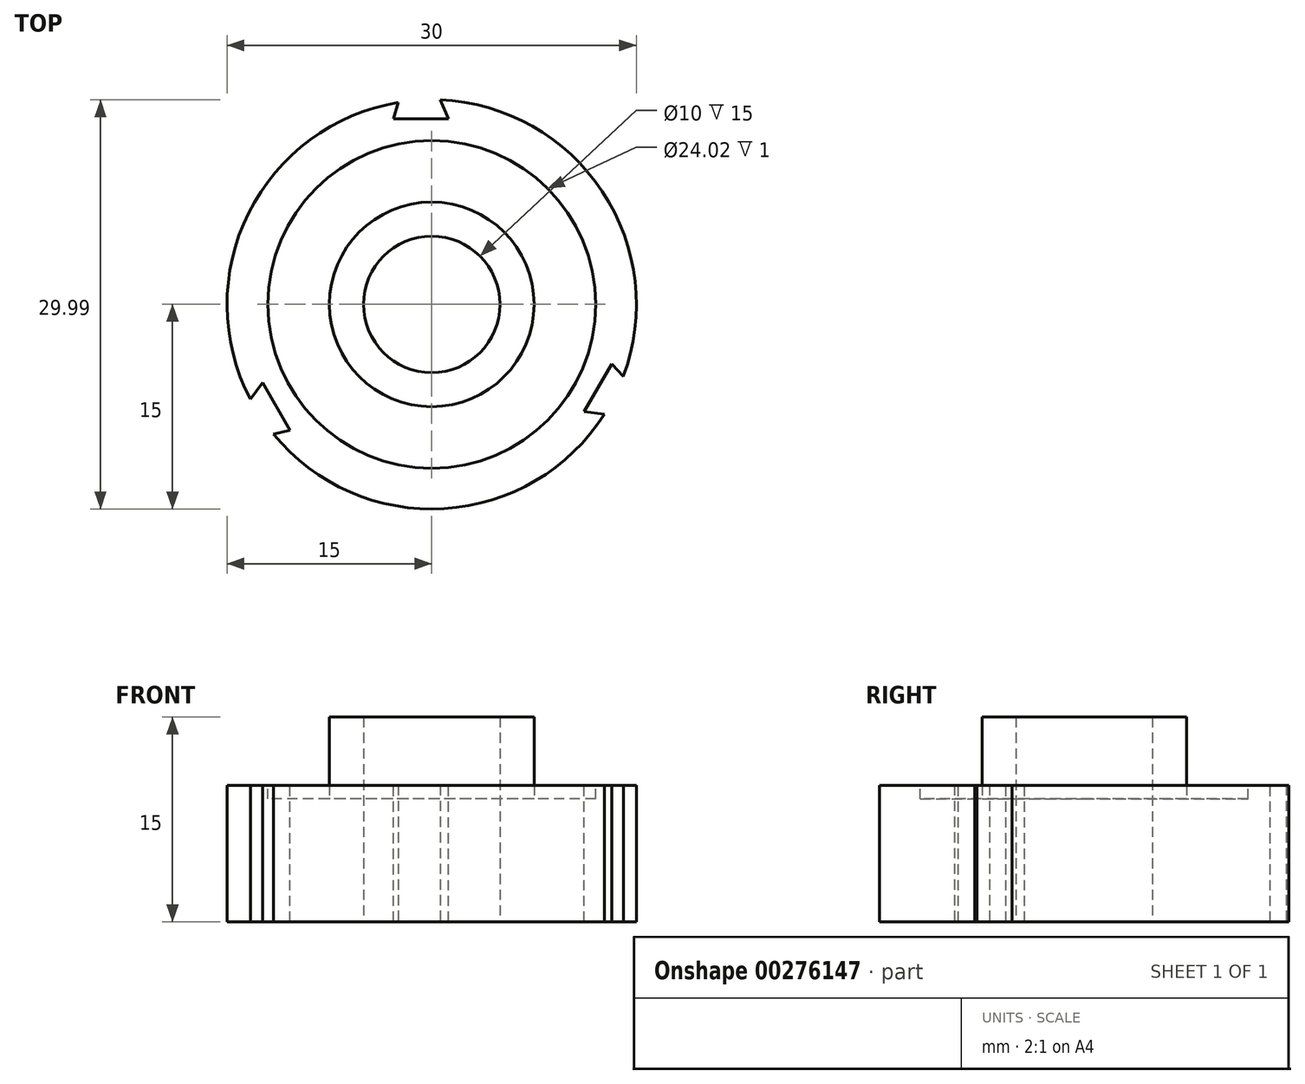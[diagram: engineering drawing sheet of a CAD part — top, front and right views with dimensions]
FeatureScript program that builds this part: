
annotation { "Feature Type Name" : "Feature", "Feature Type Description" : "" }
export const myFeature = defineFeature(function(context is Context, id is Id, definition is map)
    precondition{}
    {
        {
            var Q0;
            Q0=qCreatedBy(makeId("Top.planeOp"),FACE);
            var sketch = newSketch(context, id + "F0", { "sketchPlane" : qUnion([Q0])});
            skCircle(sketch, "E0", {"center": v(0, 0) * mm, "radius": 15 * mm});
            skCircle(sketch, "E1", {"center": v(0, 0) * mm, "radius": 5 * mm});
            skSolve(sketch);
        }
        {
            var Q0;
            Q0 = qSketchRegion(id + "F0", true);
            extrude(context, id + "F1", {"entities" : qUnion([Q0]), "depth" : 10 * mm});
        }
        {
            var Q0;
            Q0=makeQuery(id+"F1.opExtrude","CAP_FACE",FACE,{"disambiguationData":[OSD([sQuery(id+"F0.wireOp",EDGE,"E0"),sQuery(id+"F0.wireOp",EDGE,"E1")])],"isStart":false});
            var sketch = newSketch(context, id + "F2", { "sketchPlane" : qUnion([Q0])});
            skCircle(sketch, "E2", {"center": v(0, 0) * mm, "radius": 7.5 * mm});
            skCircle(sketch, "E3", {"center": v(0, 0) * mm, "radius": 5 * mm});
            skSolve(sketch);
        }
        {
            var Q0;
            Q0=makeQuery(id+"F2.imprint","IMPRINT",FACE,{"disambiguationData":[TD([[makeQuery(id+"F2.imprint","IMPRINT",EDGE,{"derivedFrom":sQuery(id+"F2.wireOp",EDGE,"E2")}),1.0]])]});
            extrude(context, id + "F3", {"entities" : qUnion([Q0]), "operationType" : NewBodyOperationType.ADD, "depth" : 5 * mm});
        }
        {
            var Q0;
            Q0=makeQuery(id+"F1.opExtrude","CAP_FACE",FACE,{"disambiguationData":[OSD([sQuery(id+"F0.wireOp",EDGE,"E0"),sQuery(id+"F0.wireOp",EDGE,"E1")])],"isStart":false});
            var sketch = newSketch(context, id + "F4", { "sketchPlane" : qUnion([Q0])});
            skCircle(sketch, "E4", {"center": v(0, 0) * mm, "radius": 12.01 * mm});
            skCircle(sketch, "E5", {"center": v(0, 0) * mm, "radius": 11.23 * mm});
            skSolve(sketch);
        }
        {
            var Q0;
            Q0=makeQuery(id+"F4.imprint","IMPRINT",FACE,{"disambiguationData":[TD([[makeQuery(id+"F4.imprint","IMPRINT",EDGE,{"derivedFrom":sQuery(id+"F4.wireOp",EDGE,"E5")}),1.0]])]});
            var Q1;
            Q1=makeQuery(id+"F4.imprint","IMPRINT",FACE,{"disambiguationData":[TD([[makeQuery(id+"F4.imprint","IMPRINT",EDGE,{"derivedFrom":sQuery(id+"F4.wireOp",EDGE,"E4")}),1.0]])]});
            extrude(context, id + "F5", {"entities" : qUnion([Q0, Q1]), "operationType" : NewBodyOperationType.REMOVE, "oppositeDirection" : true, "depth" : 1 * mm});
        }
        {
            var Q0;
            Q0=makeQuery(id+"F1.opExtrude","CAP_FACE",FACE,{"disambiguationData":[OSD([sQuery(id+"F0.wireOp",EDGE,"E0"),sQuery(id+"F0.wireOp",EDGE,"E1")])],"isStart":false});
            var sketch = newSketch(context, id + "F6", { "sketchPlane" : qUnion([Q0])});
            skLineSegment(sketch, "E6", {"start": v(-2.8, 13.62) * mm, "end": v(-1.95, 16.45) * mm});
            skLineSegment(sketch, "E7", {"start": v(-1.95, 16.45) * mm, "end": v(0, 16.45) * mm});
            skLineSegment(sketch, "E8", {"start": v(0, 16.45) * mm, "end": v(1.23, 13.62) * mm});
            skLineSegment(sketch, "E9", {"start": v(-2.8, 13.62) * mm, "end": v(1.23, 13.62) * mm});
            skLineSegment(sketch, "E10.1.0", {"start": v(-14.24, -8.22) * mm, "end": v(-12.4, -5.75) * mm});
            skLineSegment(sketch, "E10.1.1", {"start": v(-10.4, -9.24) * mm, "end": v(-13.27, -9.9) * mm});
            skLineSegment(sketch, "E10.1.2", {"start": v(-10.4, -9.24) * mm, "end": v(-12.4, -5.75) * mm});
            skLineSegment(sketch, "E10.1.3", {"start": v(-13.27, -9.9) * mm, "end": v(-14.24, -8.22) * mm});
            skLineSegment(sketch, "E10.2.0", {"start": v(14.24, -8.22) * mm, "end": v(11.18, -7.87) * mm});
            skLineSegment(sketch, "E10.2.1", {"start": v(13.2, -4.38) * mm, "end": v(15.22, -6.54) * mm});
            skLineSegment(sketch, "E10.2.2", {"start": v(13.2, -4.38) * mm, "end": v(11.18, -7.87) * mm});
            skLineSegment(sketch, "E10.2.3", {"start": v(15.22, -6.54) * mm, "end": v(14.24, -8.22) * mm});
            skPoint(sketch, "E10.center", {"position": v(0, 0) * mm});
            skSolve(sketch);
        }
        {
            var Q0;
            Q0 = qSketchRegion(id + "F6", true);
            extrude(context, id + "F7", {"entities" : qUnion([Q0]), "operationType" : NewBodyOperationType.REMOVE, "oppositeDirection" : true, "depth" : 25 * mm});
        }
    });
